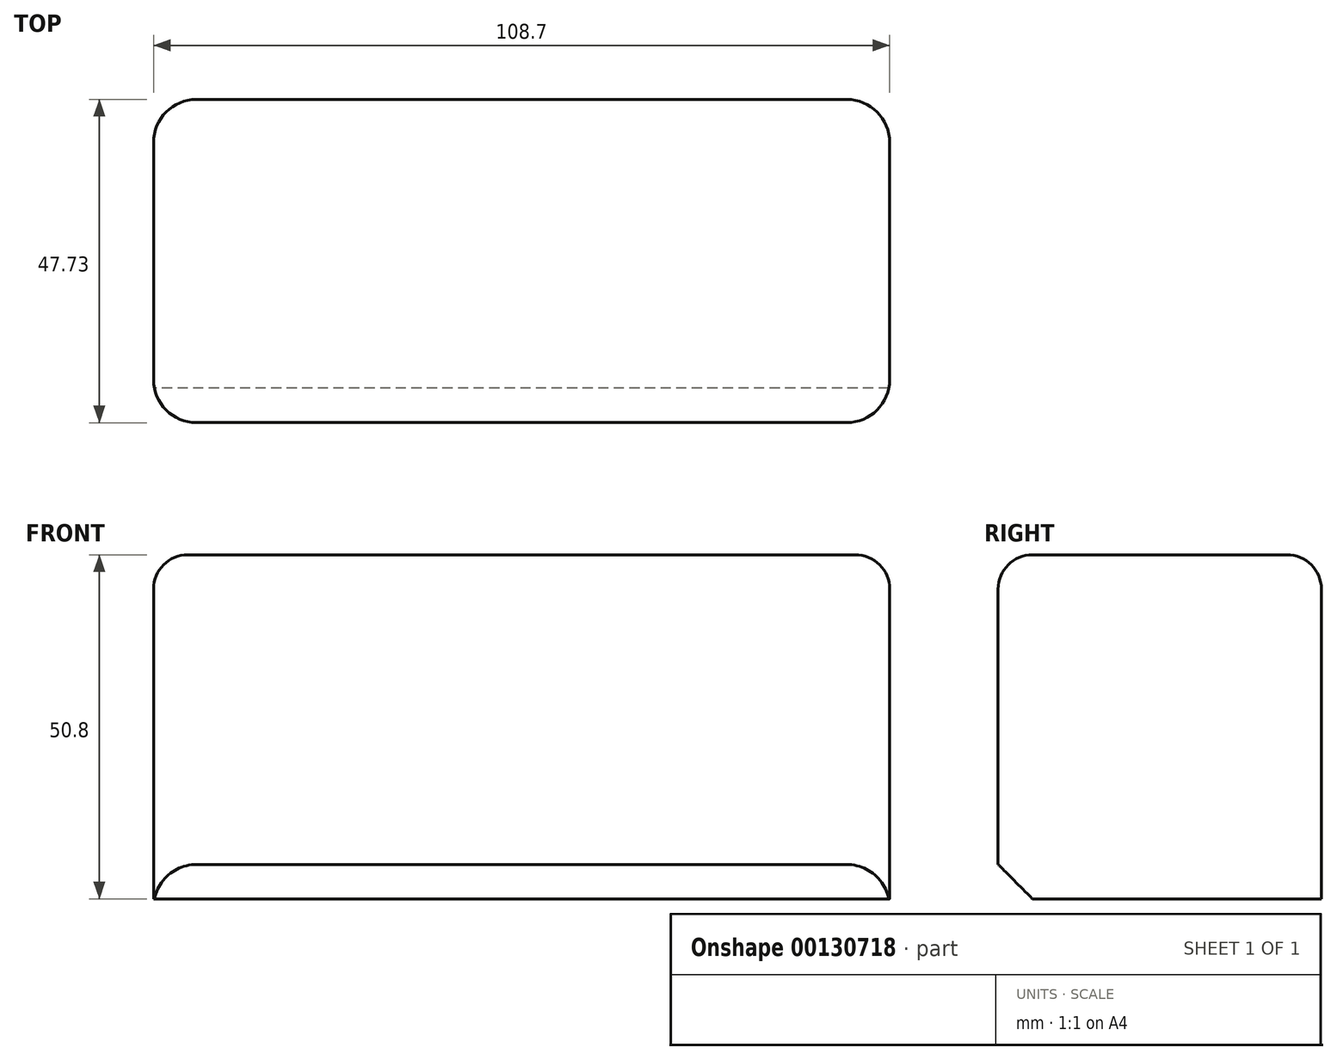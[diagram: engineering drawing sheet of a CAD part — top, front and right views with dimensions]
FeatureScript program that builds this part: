
annotation { "Feature Type Name" : "Feature", "Feature Type Description" : "" }
export const myFeature = defineFeature(function(context is Context, id is Id, definition is map)
    precondition{}
    {
        {
            var Q0;
            Q0=qCreatedBy(makeId("Top.planeOp"),FACE);
            var sketch = newSketch(context, id + "F0", { "sketchPlane" : qUnion([Q0])});
            skLineSegment(sketch, "E0.bottom", {"start": v(-48, 0) * mm, "end": v(48, 0) * mm});
            skLineSegment(sketch, "E0.top", {"start": v(-48, -47.73) * mm, "end": v(48, -47.73) * mm});
            skLineSegment(sketch, "E0.left", {"start": v(-54.35, -6.35) * mm, "end": v(-54.35, -41.38) * mm});
            skLineSegment(sketch, "E0.right", {"start": v(54.35, -6.35) * mm, "end": v(54.35, -41.38) * mm});
            skPoint(sketch, "E1.visualSharp", {"position": v(-54.35, 0) * mm});
            skArc(sketch, "E1.filletArc", {"start": v(-48, 0) * mm, "mid": v(-52.49, -1.86) * mm, "end": v(-54.35, -6.35) * mm});
            skPoint(sketch, "E2.visualSharp", {"position": v(54.35, 0) * mm});
            skArc(sketch, "E2.filletArc", {"start": v(54.35, -6.35) * mm, "mid": v(52.49, -1.86) * mm, "end": v(48, 0) * mm});
            skPoint(sketch, "E3.visualSharp", {"position": v(54.35, -47.73) * mm});
            skArc(sketch, "E3.filletArc", {"start": v(48, -47.73) * mm, "mid": v(52.49, -45.87) * mm, "end": v(54.35, -41.38) * mm});
            skPoint(sketch, "E4.visualSharp", {"position": v(-54.35, -47.73) * mm});
            skArc(sketch, "E4.filletArc", {"start": v(-54.35, -41.38) * mm, "mid": v(-52.49, -45.87) * mm, "end": v(-48, -47.73) * mm});
            skSolve(sketch);
        }
        {
            var Q0;
            Q0 = qSketchRegion(id + "F0", true);
            extrude(context, id + "F1", {"entities" : qUnion([Q0]), "depth" : 25.4 * mm, "hasSecondDirection" : true, "secondDirectionOppositeDirection" : true, "secondDirectionDepth" : 25.4 * mm});
        }
        {
            var Q0;
            Q0=makeQuery(id+"F1.opExtrude","CAP_EDGE",EDGE,{"disambiguationData":[OSD([sQuery(id+"F0.wireOp",EDGE,"E0.top")])],"isStart":false});
            fillet(context, id + "F2", {"entities" : qUnion([Q0]), "radius" : 5.08 * mm, "tangentPropagation" : true, "allowEdgeOverflow" : false});
        }
        {
            var Q0;
            Q0=makeQuery(id+"F1.opExtrude","CAP_EDGE",EDGE,{"disambiguationData":[OSD([sQuery(id+"F0.wireOp",EDGE,"E0.top")])],"isStart":true});
            chamfer(context, id + "F3", {"entities" : qUnion([Q0]), "width" : 5.08 * mm});
        }
    });
